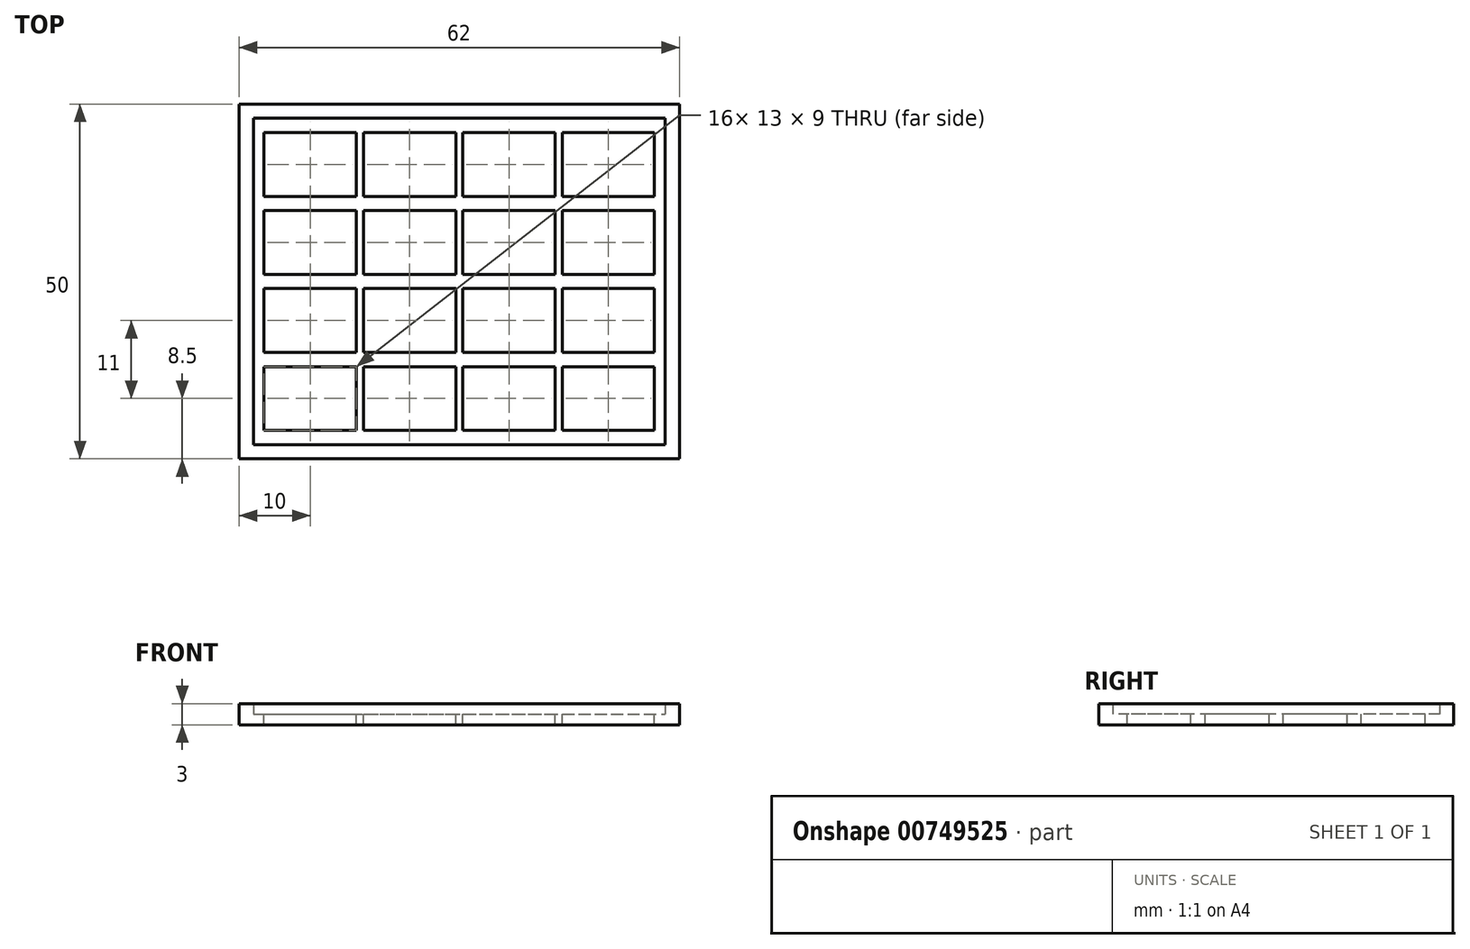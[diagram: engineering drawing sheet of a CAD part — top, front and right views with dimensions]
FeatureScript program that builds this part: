
annotation { "Feature Type Name" : "Feature", "Feature Type Description" : "" }
export const myFeature = defineFeature(function(context is Context, id is Id, definition is map)
    precondition{}
    {
        {
            var Q0;
            Q0=qCreatedBy(makeId("Top.planeOp"),FACE);
            var sketch = newSketch(context, id + "F0", { "sketchPlane" : qUnion([Q0])});
            skLineSegment(sketch, "E0.bottom", {"start": v(-29, 23) * mm, "end": v(29, 23) * mm});
            skLineSegment(sketch, "E0.top", {"start": v(-29, -23) * mm, "end": v(29, -23) * mm});
            skLineSegment(sketch, "E0.left", {"start": v(-29, 23) * mm, "end": v(-29, -23) * mm});
            skLineSegment(sketch, "E0.right", {"start": v(29, 23) * mm, "end": v(29, -23) * mm});
            skLineSegment(sketch, "E1.bottom", {"start": v(-31, 25) * mm, "end": v(31, 25) * mm});
            skLineSegment(sketch, "E1.top", {"start": v(-31, -25) * mm, "end": v(31, -25) * mm});
            skLineSegment(sketch, "E1.left", {"start": v(-31, 25) * mm, "end": v(-31, -25) * mm});
            skLineSegment(sketch, "E1.right", {"start": v(31, 25) * mm, "end": v(31, -25) * mm});
            skSolve(sketch);
        }
        {
            var Q0;
            Q0=makeQuery(id+"F0.imprint","IMPRINT",FACE,{"disambiguationData":[TD([[makeQuery(id+"F0.imprint","IMPRINT",EDGE,{"derivedFrom":sQuery(id+"F0.wireOp",EDGE,"E0.bottom")}),-1.0]])]});
            extrude(context, id + "F1", {"entities" : qUnion([Q0]), "depth" : 1.5 * mm, "offsetDistance" : 25 * mm});
        }
        {
            var Q0;
            Q0=makeQuery(id+"F1.opExtrude","CAP_FACE",FACE,{"disambiguationData":[OSD([sQuery(id+"F0.wireOp",EDGE,"E0.bottom"),sQuery(id+"F0.wireOp",EDGE,"E0.top"),sQuery(id+"F0.wireOp",EDGE,"E0.left"),sQuery(id+"F0.wireOp",EDGE,"E0.right")])],"isStart":false});
            var sketch = newSketch(context, id + "F2", { "sketchPlane" : qUnion([Q0])});
            skPoint(sketch, "E2.middle", {"position": v(0, 0) * mm});
            skLineSegment(sketch, "E3.bottom", {"start": v(-15.5, 13) * mm, "end": v(-26.5, 13) * mm});
            skLineSegment(sketch, "E3.top", {"start": v(-15.5, 20) * mm, "end": v(-26.5, 20) * mm});
            skLineSegment(sketch, "E3.left", {"start": v(-15.5, 13) * mm, "end": v(-15.5, 20) * mm});
            skLineSegment(sketch, "E3.right", {"start": v(-26.5, 13) * mm, "end": v(-26.5, 20) * mm});
            skPoint(sketch, "E3.middle", {"position": v(-21, 16.5) * mm});
            skLineSegment(sketch, "E4.1.0.0", {"start": v(-12.5, 13) * mm, "end": v(-12.5, 20) * mm});
            skLineSegment(sketch, "E4.1.0.1", {"start": v(-1.5, 13) * mm, "end": v(-1.5, 20) * mm});
            skLineSegment(sketch, "E4.1.0.2", {"start": v(-1.5, 20) * mm, "end": v(-12.5, 20) * mm});
            skPoint(sketch, "E4.1.0.3", {"position": v(-7, 16.5) * mm});
            skLineSegment(sketch, "E4.1.0.4", {"start": v(-1.5, 13) * mm, "end": v(-12.5, 13) * mm});
            skLineSegment(sketch, "E4.2.0.0", {"start": v(1.5, 13) * mm, "end": v(1.5, 20) * mm});
            skLineSegment(sketch, "E4.2.0.1", {"start": v(12.5, 13) * mm, "end": v(12.5, 20) * mm});
            skLineSegment(sketch, "E4.2.0.2", {"start": v(12.5, 20) * mm, "end": v(1.5, 20) * mm});
            skPoint(sketch, "E4.2.0.3", {"position": v(7, 16.5) * mm});
            skLineSegment(sketch, "E4.2.0.4", {"start": v(12.5, 13) * mm, "end": v(1.5, 13) * mm});
            skLineSegment(sketch, "E4.3.0.0", {"start": v(15.5, 13) * mm, "end": v(15.5, 20) * mm});
            skLineSegment(sketch, "E4.3.0.1", {"start": v(26.5, 13) * mm, "end": v(26.5, 20) * mm});
            skLineSegment(sketch, "E4.3.0.2", {"start": v(26.5, 20) * mm, "end": v(15.5, 20) * mm});
            skPoint(sketch, "E4.3.0.3", {"position": v(21, 16.5) * mm});
            skLineSegment(sketch, "E4.3.0.4", {"start": v(26.5, 13) * mm, "end": v(15.5, 13) * mm});
            skLineSegment(sketch, "E4.direction1", {"start": v(-26.5, 13) * mm, "end": v(-12.5, 13) * mm, "construction": true});
            skLineSegment(sketch, "E5.1.0.0", {"start": v(15.58, 2) * mm, "end": v(15.58, 9) * mm});
            skLineSegment(sketch, "E5.1.0.1", {"start": v(26.58, 9) * mm, "end": v(15.58, 9) * mm});
            skLineSegment(sketch, "E5.1.0.2", {"start": v(-26.42, 2) * mm, "end": v(-12.42, 2) * mm, "construction": true});
            skPoint(sketch, "E5.1.0.3", {"position": v(-20.92, 5.5) * mm});
            skLineSegment(sketch, "E5.1.0.4", {"start": v(1.58, 2) * mm, "end": v(1.58, 9) * mm});
            skLineSegment(sketch, "E5.1.0.5", {"start": v(-1.42, 2) * mm, "end": v(-12.42, 2) * mm});
            skLineSegment(sketch, "E5.1.0.6", {"start": v(-1.42, 9) * mm, "end": v(-12.42, 9) * mm});
            skLineSegment(sketch, "E5.1.0.7", {"start": v(-1.42, 2) * mm, "end": v(-1.42, 9) * mm});
            skLineSegment(sketch, "E5.1.0.8", {"start": v(-12.42, 2) * mm, "end": v(-12.42, 9) * mm});
            skLineSegment(sketch, "E5.1.0.9", {"start": v(-26.42, 2) * mm, "end": v(-26.42, 9) * mm});
            skLineSegment(sketch, "E5.1.0.10", {"start": v(-15.42, 2) * mm, "end": v(-15.42, 9) * mm});
            skLineSegment(sketch, "E5.1.0.11", {"start": v(-15.42, 9) * mm, "end": v(-26.42, 9) * mm});
            skPoint(sketch, "E5.1.0.12", {"position": v(7.08, 5.5) * mm});
            skLineSegment(sketch, "E5.1.0.13", {"start": v(12.58, 2) * mm, "end": v(1.58, 2) * mm});
            skLineSegment(sketch, "E5.1.0.14", {"start": v(12.58, 9) * mm, "end": v(1.58, 9) * mm});
            skLineSegment(sketch, "E5.1.0.15", {"start": v(12.58, 2) * mm, "end": v(12.58, 9) * mm});
            skLineSegment(sketch, "E5.1.0.16", {"start": v(26.58, 2) * mm, "end": v(26.58, 9) * mm});
            skLineSegment(sketch, "E5.1.0.17", {"start": v(26.58, 2) * mm, "end": v(15.58, 2) * mm});
            skPoint(sketch, "E5.1.0.18", {"position": v(-6.92, 5.5) * mm});
            skPoint(sketch, "E5.1.0.19", {"position": v(21.08, 5.5) * mm});
            skLineSegment(sketch, "E5.1.0.20", {"start": v(-15.42, 2) * mm, "end": v(-26.42, 2) * mm});
            skLineSegment(sketch, "E5.2.0.0", {"start": v(15.65, -9) * mm, "end": v(15.65, -2) * mm});
            skLineSegment(sketch, "E5.2.0.1", {"start": v(26.65, -2) * mm, "end": v(15.65, -2) * mm});
            skLineSegment(sketch, "E5.2.0.2", {"start": v(-26.35, -9) * mm, "end": v(-12.35, -9) * mm, "construction": true});
            skPoint(sketch, "E5.2.0.3", {"position": v(-20.85, -5.5) * mm});
            skLineSegment(sketch, "E5.2.0.4", {"start": v(1.65, -9) * mm, "end": v(1.65, -2) * mm});
            skLineSegment(sketch, "E5.2.0.5", {"start": v(-1.35, -9) * mm, "end": v(-12.35, -9) * mm});
            skLineSegment(sketch, "E5.2.0.6", {"start": v(-1.35, -2) * mm, "end": v(-12.35, -2) * mm});
            skLineSegment(sketch, "E5.2.0.7", {"start": v(-1.35, -9) * mm, "end": v(-1.35, -2) * mm});
            skLineSegment(sketch, "E5.2.0.8", {"start": v(-12.35, -9) * mm, "end": v(-12.35, -2) * mm});
            skLineSegment(sketch, "E5.2.0.9", {"start": v(-26.35, -9) * mm, "end": v(-26.35, -2) * mm});
            skLineSegment(sketch, "E5.2.0.10", {"start": v(-15.35, -9) * mm, "end": v(-15.35, -2) * mm});
            skLineSegment(sketch, "E5.2.0.11", {"start": v(-15.35, -2) * mm, "end": v(-26.35, -2) * mm});
            skPoint(sketch, "E5.2.0.12", {"position": v(7.15, -5.5) * mm});
            skLineSegment(sketch, "E5.2.0.13", {"start": v(12.65, -9) * mm, "end": v(1.65, -9) * mm});
            skLineSegment(sketch, "E5.2.0.14", {"start": v(12.65, -2) * mm, "end": v(1.65, -2) * mm});
            skLineSegment(sketch, "E5.2.0.15", {"start": v(12.65, -9) * mm, "end": v(12.65, -2) * mm});
            skLineSegment(sketch, "E5.2.0.16", {"start": v(26.65, -9) * mm, "end": v(26.65, -2) * mm});
            skLineSegment(sketch, "E5.2.0.17", {"start": v(26.65, -9) * mm, "end": v(15.65, -9) * mm});
            skPoint(sketch, "E5.2.0.18", {"position": v(-6.85, -5.5) * mm});
            skPoint(sketch, "E5.2.0.19", {"position": v(21.15, -5.5) * mm});
            skLineSegment(sketch, "E5.2.0.20", {"start": v(-15.35, -9) * mm, "end": v(-26.35, -9) * mm});
            skLineSegment(sketch, "E5.3.0.0", {"start": v(15.73, -20) * mm, "end": v(15.73, -13) * mm});
            skLineSegment(sketch, "E5.3.0.1", {"start": v(26.73, -13) * mm, "end": v(15.73, -13) * mm});
            skLineSegment(sketch, "E5.3.0.2", {"start": v(-26.27, -20) * mm, "end": v(-12.27, -20) * mm, "construction": true});
            skPoint(sketch, "E5.3.0.3", {"position": v(-20.77, -16.5) * mm});
            skLineSegment(sketch, "E5.3.0.4", {"start": v(1.73, -20) * mm, "end": v(1.73, -13) * mm});
            skLineSegment(sketch, "E5.3.0.5", {"start": v(-1.27, -20) * mm, "end": v(-12.27, -20) * mm});
            skLineSegment(sketch, "E5.3.0.6", {"start": v(-1.27, -13) * mm, "end": v(-12.27, -13) * mm});
            skLineSegment(sketch, "E5.3.0.7", {"start": v(-1.27, -20) * mm, "end": v(-1.27, -13) * mm});
            skLineSegment(sketch, "E5.3.0.8", {"start": v(-12.27, -20) * mm, "end": v(-12.27, -13) * mm});
            skLineSegment(sketch, "E5.3.0.9", {"start": v(-26.27, -20) * mm, "end": v(-26.27, -13) * mm});
            skLineSegment(sketch, "E5.3.0.10", {"start": v(-15.27, -20) * mm, "end": v(-15.27, -13) * mm});
            skLineSegment(sketch, "E5.3.0.11", {"start": v(-15.27, -13) * mm, "end": v(-26.27, -13) * mm});
            skPoint(sketch, "E5.3.0.12", {"position": v(7.23, -16.5) * mm});
            skLineSegment(sketch, "E5.3.0.13", {"start": v(12.73, -20) * mm, "end": v(1.73, -20) * mm});
            skLineSegment(sketch, "E5.3.0.14", {"start": v(12.73, -13) * mm, "end": v(1.73, -13) * mm});
            skLineSegment(sketch, "E5.3.0.15", {"start": v(12.73, -20) * mm, "end": v(12.73, -13) * mm});
            skLineSegment(sketch, "E5.3.0.16", {"start": v(26.73, -20) * mm, "end": v(26.73, -13) * mm});
            skLineSegment(sketch, "E5.3.0.17", {"start": v(26.73, -20) * mm, "end": v(15.73, -20) * mm});
            skPoint(sketch, "E5.3.0.18", {"position": v(-6.77, -16.5) * mm});
            skPoint(sketch, "E5.3.0.19", {"position": v(21.23, -16.5) * mm});
            skLineSegment(sketch, "E5.3.0.20", {"start": v(-15.27, -20) * mm, "end": v(-26.27, -20) * mm});
            skLineSegment(sketch, "E5.direction1", {"start": v(-26.5, 13) * mm, "end": v(-26.42, 2) * mm, "construction": true});
            skSolve(sketch);
        }
        {
            var Q0;
            Q0=makeQuery(id+"F2.imprint","IMPRINT",FACE,{"disambiguationData":[TD([[makeQuery(id+"F2.imprint","IMPRINT",EDGE,{"derivedFrom":sQuery(id+"F2.wireOp",EDGE,"E3.bottom")}),-1.0]])]});
            var Q1;
            Q1=makeQuery(id+"F2.imprint","IMPRINT",FACE,{"disambiguationData":[TD([[makeQuery(id+"F2.imprint","IMPRINT",EDGE,{"derivedFrom":sQuery(id+"F2.wireOp",EDGE,"E4.1.0.0")}),-1.0]])]});
            var Q2;
            Q2=makeQuery(id+"F2.imprint","IMPRINT",FACE,{"disambiguationData":[TD([[makeQuery(id+"F2.imprint","IMPRINT",EDGE,{"derivedFrom":sQuery(id+"F2.wireOp",EDGE,"E4.2.0.0")}),-1.0]])]});
            var Q3;
            Q3=makeQuery(id+"F2.imprint","IMPRINT",FACE,{"disambiguationData":[TD([[makeQuery(id+"F2.imprint","IMPRINT",EDGE,{"derivedFrom":sQuery(id+"F2.wireOp",EDGE,"E4.3.0.0")}),-1.0]])]});
            var Q4;
            Q4=makeQuery(id+"F2.imprint","IMPRINT",FACE,{"disambiguationData":[TD([[makeQuery(id+"F2.imprint","IMPRINT",EDGE,{"derivedFrom":sQuery(id+"F2.wireOp",EDGE,"E5.1.0.9")}),-1.0]])]});
            var Q5;
            Q5=makeQuery(id+"F2.imprint","IMPRINT",FACE,{"disambiguationData":[TD([[makeQuery(id+"F2.imprint","IMPRINT",EDGE,{"derivedFrom":sQuery(id+"F2.wireOp",EDGE,"E5.1.0.5")}),-1.0]])]});
            var Q6;
            Q6=makeQuery(id+"F2.imprint","IMPRINT",FACE,{"disambiguationData":[TD([[makeQuery(id+"F2.imprint","IMPRINT",EDGE,{"derivedFrom":sQuery(id+"F2.wireOp",EDGE,"E5.1.0.4")}),-1.0]])]});
            var Q7;
            Q7=makeQuery(id+"F2.imprint","IMPRINT",FACE,{"disambiguationData":[TD([[makeQuery(id+"F2.imprint","IMPRINT",EDGE,{"derivedFrom":sQuery(id+"F2.wireOp",EDGE,"E5.1.0.0")}),-1.0]])]});
            var Q8;
            Q8=makeQuery(id+"F2.imprint","IMPRINT",FACE,{"disambiguationData":[TD([[makeQuery(id+"F2.imprint","IMPRINT",EDGE,{"derivedFrom":sQuery(id+"F2.wireOp",EDGE,"E5.2.0.9")}),-1.0]])]});
            var Q9;
            Q9=makeQuery(id+"F2.imprint","IMPRINT",FACE,{"disambiguationData":[TD([[makeQuery(id+"F2.imprint","IMPRINT",EDGE,{"derivedFrom":sQuery(id+"F2.wireOp",EDGE,"E5.2.0.5")}),-1.0]])]});
            var Q10;
            Q10=makeQuery(id+"F2.imprint","IMPRINT",FACE,{"disambiguationData":[TD([[makeQuery(id+"F2.imprint","IMPRINT",EDGE,{"derivedFrom":sQuery(id+"F2.wireOp",EDGE,"E5.2.0.4")}),-1.0]])]});
            var Q11;
            Q11=makeQuery(id+"F2.imprint","IMPRINT",FACE,{"disambiguationData":[TD([[makeQuery(id+"F2.imprint","IMPRINT",EDGE,{"derivedFrom":sQuery(id+"F2.wireOp",EDGE,"E5.2.0.0")}),-1.0]])]});
            var Q12;
            Q12=makeQuery(id+"F2.imprint","IMPRINT",FACE,{"disambiguationData":[TD([[makeQuery(id+"F2.imprint","IMPRINT",EDGE,{"derivedFrom":sQuery(id+"F2.wireOp",EDGE,"E5.3.0.9")}),-1.0]])]});
            var Q13;
            Q13=makeQuery(id+"F2.imprint","IMPRINT",FACE,{"disambiguationData":[TD([[makeQuery(id+"F2.imprint","IMPRINT",EDGE,{"derivedFrom":sQuery(id+"F2.wireOp",EDGE,"E5.3.0.5")}),-1.0]])]});
            var Q14;
            Q14=makeQuery(id+"F2.imprint","IMPRINT",FACE,{"disambiguationData":[TD([[makeQuery(id+"F2.imprint","IMPRINT",EDGE,{"derivedFrom":sQuery(id+"F2.wireOp",EDGE,"E5.3.0.4")}),-1.0]])]});
            var Q15;
            Q15=makeQuery(id+"F2.imprint","IMPRINT",FACE,{"disambiguationData":[TD([[makeQuery(id+"F2.imprint","IMPRINT",EDGE,{"derivedFrom":sQuery(id+"F2.wireOp",EDGE,"E5.3.0.0")}),-1.0]])]});
            extrude(context, id + "F3", {"entities" : qUnion([Q0, Q1, Q2, Q3, Q4, Q5, Q6, Q7, Q8, Q9, Q10, Q11, Q12, Q13, Q14, Q15]), "operationType" : NewBodyOperationType.REMOVE, "endBound" : BoundingType.THROUGH_ALL, "oppositeDirection" : true, "depth" : 4 * mm, "offsetDistance" : 25 * mm});
        }
        {
            var Q0;
            Q0=makeQuery(id+"F1.opExtrude","CAP_FACE",FACE,{"disambiguationData":[OSD([sQuery(id+"F0.wireOp",EDGE,"E0.bottom"),sQuery(id+"F0.wireOp",EDGE,"E0.top"),sQuery(id+"F0.wireOp",EDGE,"E0.left"),sQuery(id+"F0.wireOp",EDGE,"E0.right")])],"isStart":false});
            var sketch = newSketch(context, id + "F4", { "sketchPlane" : qUnion([Q0])});
            skLineSegment(sketch, "E6.bottom", {"start": v(-27.5, 21) * mm, "end": v(-14.5, 21) * mm});
            skLineSegment(sketch, "E6.top", {"start": v(-27.5, 12) * mm, "end": v(-14.5, 12) * mm});
            skLineSegment(sketch, "E6.left", {"start": v(-27.5, 21) * mm, "end": v(-27.5, 12) * mm});
            skLineSegment(sketch, "E6.right", {"start": v(-14.5, 21) * mm, "end": v(-14.5, 12) * mm});
            skLineSegment(sketch, "E7.1.0.0", {"start": v(-13.5, 12) * mm, "end": v(-0.5, 12) * mm});
            skLineSegment(sketch, "E7.1.0.1", {"start": v(-13.5, 21) * mm, "end": v(-0.5, 21) * mm});
            skLineSegment(sketch, "E7.1.0.2", {"start": v(-13.5, 21) * mm, "end": v(-13.5, 12) * mm});
            skLineSegment(sketch, "E7.1.0.3", {"start": v(-0.5, 21) * mm, "end": v(-0.5, 12) * mm});
            skLineSegment(sketch, "E7.2.0.0", {"start": v(0.5, 12) * mm, "end": v(13.5, 12) * mm});
            skLineSegment(sketch, "E7.2.0.1", {"start": v(0.5, 21) * mm, "end": v(13.5, 21) * mm});
            skLineSegment(sketch, "E7.2.0.2", {"start": v(0.5, 21) * mm, "end": v(0.5, 12) * mm});
            skLineSegment(sketch, "E7.2.0.3", {"start": v(13.5, 21) * mm, "end": v(13.5, 12) * mm});
            skLineSegment(sketch, "E7.3.0.0", {"start": v(14.5, 12) * mm, "end": v(27.5, 12) * mm});
            skLineSegment(sketch, "E7.3.0.1", {"start": v(14.5, 21) * mm, "end": v(27.5, 21) * mm});
            skLineSegment(sketch, "E7.3.0.2", {"start": v(14.5, 21) * mm, "end": v(14.5, 12) * mm});
            skLineSegment(sketch, "E7.3.0.3", {"start": v(27.5, 21) * mm, "end": v(27.5, 12) * mm});
            skLineSegment(sketch, "E7.direction1", {"start": v(-27.5, 12) * mm, "end": v(-13.5, 12) * mm, "construction": true});
            skLineSegment(sketch, "E8.1.0.0", {"start": v(14.5, 1) * mm, "end": v(27.5, 1) * mm});
            skLineSegment(sketch, "E8.1.0.1", {"start": v(13.5, 10) * mm, "end": v(13.5, 1) * mm});
            skLineSegment(sketch, "E8.1.0.2", {"start": v(0.5, 10) * mm, "end": v(0.5, 1) * mm});
            skLineSegment(sketch, "E8.1.0.3", {"start": v(0.5, 10) * mm, "end": v(13.5, 10) * mm});
            skLineSegment(sketch, "E8.1.0.4", {"start": v(0.5, 1) * mm, "end": v(13.5, 1) * mm});
            skLineSegment(sketch, "E8.1.0.5", {"start": v(-0.5, 10) * mm, "end": v(-0.5, 1) * mm});
            skLineSegment(sketch, "E8.1.0.6", {"start": v(-13.5, 10) * mm, "end": v(-13.5, 1) * mm});
            skLineSegment(sketch, "E8.1.0.7", {"start": v(-13.5, 10) * mm, "end": v(-0.5, 10) * mm});
            skLineSegment(sketch, "E8.1.0.8", {"start": v(-14.5, 10) * mm, "end": v(-14.5, 1) * mm});
            skLineSegment(sketch, "E8.1.0.9", {"start": v(-27.5, 10) * mm, "end": v(-27.5, 1) * mm});
            skLineSegment(sketch, "E8.1.0.10", {"start": v(-27.5, 10) * mm, "end": v(-14.5, 10) * mm});
            skLineSegment(sketch, "E8.1.0.11", {"start": v(27.5, 10) * mm, "end": v(27.5, 1) * mm});
            skLineSegment(sketch, "E8.1.0.12", {"start": v(14.5, 10) * mm, "end": v(14.5, 1) * mm});
            skLineSegment(sketch, "E8.1.0.13", {"start": v(14.5, 10) * mm, "end": v(27.5, 10) * mm});
            skLineSegment(sketch, "E8.1.0.14", {"start": v(-27.5, 1) * mm, "end": v(-13.5, 1) * mm, "construction": true});
            skLineSegment(sketch, "E8.1.0.15", {"start": v(-27.5, 1) * mm, "end": v(-14.5, 1) * mm});
            skLineSegment(sketch, "E8.1.0.16", {"start": v(-13.5, 1) * mm, "end": v(-0.5, 1) * mm});
            skLineSegment(sketch, "E8.2.0.0", {"start": v(14.5, -10) * mm, "end": v(27.5, -10) * mm});
            skLineSegment(sketch, "E8.2.0.1", {"start": v(13.5, -1) * mm, "end": v(13.5, -10) * mm});
            skLineSegment(sketch, "E8.2.0.2", {"start": v(0.5, -1) * mm, "end": v(0.5, -10) * mm});
            skLineSegment(sketch, "E8.2.0.3", {"start": v(0.5, -1) * mm, "end": v(13.5, -1) * mm});
            skLineSegment(sketch, "E8.2.0.4", {"start": v(0.5, -10) * mm, "end": v(13.5, -10) * mm});
            skLineSegment(sketch, "E8.2.0.5", {"start": v(-0.5, -1) * mm, "end": v(-0.5, -10) * mm});
            skLineSegment(sketch, "E8.2.0.6", {"start": v(-13.5, -1) * mm, "end": v(-13.5, -10) * mm});
            skLineSegment(sketch, "E8.2.0.7", {"start": v(-13.5, -1) * mm, "end": v(-0.5, -1) * mm});
            skLineSegment(sketch, "E8.2.0.8", {"start": v(-14.5, -1) * mm, "end": v(-14.5, -10) * mm});
            skLineSegment(sketch, "E8.2.0.9", {"start": v(-27.5, -1) * mm, "end": v(-27.5, -10) * mm});
            skLineSegment(sketch, "E8.2.0.10", {"start": v(-27.5, -1) * mm, "end": v(-14.5, -1) * mm});
            skLineSegment(sketch, "E8.2.0.11", {"start": v(27.5, -1) * mm, "end": v(27.5, -10) * mm});
            skLineSegment(sketch, "E8.2.0.12", {"start": v(14.5, -1) * mm, "end": v(14.5, -10) * mm});
            skLineSegment(sketch, "E8.2.0.13", {"start": v(14.5, -1) * mm, "end": v(27.5, -1) * mm});
            skLineSegment(sketch, "E8.2.0.14", {"start": v(-27.5, -10) * mm, "end": v(-13.5, -10) * mm, "construction": true});
            skLineSegment(sketch, "E8.2.0.15", {"start": v(-27.5, -10) * mm, "end": v(-14.5, -10) * mm});
            skLineSegment(sketch, "E8.2.0.16", {"start": v(-13.5, -10) * mm, "end": v(-0.5, -10) * mm});
            skLineSegment(sketch, "E8.3.0.0", {"start": v(14.5, -21) * mm, "end": v(27.5, -21) * mm});
            skLineSegment(sketch, "E8.3.0.1", {"start": v(13.5, -12) * mm, "end": v(13.5, -21) * mm});
            skLineSegment(sketch, "E8.3.0.2", {"start": v(0.5, -12) * mm, "end": v(0.5, -21) * mm});
            skLineSegment(sketch, "E8.3.0.3", {"start": v(0.5, -12) * mm, "end": v(13.5, -12) * mm});
            skLineSegment(sketch, "E8.3.0.4", {"start": v(0.5, -21) * mm, "end": v(13.5, -21) * mm});
            skLineSegment(sketch, "E8.3.0.5", {"start": v(-0.5, -12) * mm, "end": v(-0.5, -21) * mm});
            skLineSegment(sketch, "E8.3.0.6", {"start": v(-13.5, -12) * mm, "end": v(-13.5, -21) * mm});
            skLineSegment(sketch, "E8.3.0.7", {"start": v(-13.5, -12) * mm, "end": v(-0.5, -12) * mm});
            skLineSegment(sketch, "E8.3.0.8", {"start": v(-14.5, -12) * mm, "end": v(-14.5, -21) * mm});
            skLineSegment(sketch, "E8.3.0.9", {"start": v(-27.5, -12) * mm, "end": v(-27.5, -21) * mm});
            skLineSegment(sketch, "E8.3.0.10", {"start": v(-27.5, -12) * mm, "end": v(-14.5, -12) * mm});
            skLineSegment(sketch, "E8.3.0.11", {"start": v(27.5, -12) * mm, "end": v(27.5, -21) * mm});
            skLineSegment(sketch, "E8.3.0.12", {"start": v(14.5, -12) * mm, "end": v(14.5, -21) * mm});
            skLineSegment(sketch, "E8.3.0.13", {"start": v(14.5, -12) * mm, "end": v(27.5, -12) * mm});
            skLineSegment(sketch, "E8.3.0.14", {"start": v(-27.5, -21) * mm, "end": v(-13.5, -21) * mm, "construction": true});
            skLineSegment(sketch, "E8.3.0.15", {"start": v(-27.5, -21) * mm, "end": v(-14.5, -21) * mm});
            skLineSegment(sketch, "E8.3.0.16", {"start": v(-13.5, -21) * mm, "end": v(-0.5, -21) * mm});
            skLineSegment(sketch, "E8.direction1", {"start": v(-27.5, 12) * mm, "end": v(-27.5, 1) * mm, "construction": true});
            skSolve(sketch);
        }
        {
            var Q0;
            Q0=makeQuery(id+"F4.imprint","IMPRINT",FACE,{"disambiguationData":[TD([[makeQuery(id+"F4.imprint","IMPRINT",EDGE,{"derivedFrom":sQuery(id+"F4.wireOp",EDGE,"E6.bottom")}),-1.0]])]});
            var Q1;
            Q1=makeQuery(id+"F4.imprint","IMPRINT",FACE,{"disambiguationData":[TD([[makeQuery(id+"F4.imprint","IMPRINT",EDGE,{"derivedFrom":sQuery(id+"F4.wireOp",EDGE,"E7.1.0.0")}),1.0]])]});
            var Q2;
            Q2=makeQuery(id+"F4.imprint","IMPRINT",FACE,{"disambiguationData":[TD([[makeQuery(id+"F4.imprint","IMPRINT",EDGE,{"derivedFrom":sQuery(id+"F4.wireOp",EDGE,"E7.2.0.0")}),1.0]])]});
            var Q3;
            Q3=makeQuery(id+"F4.imprint","IMPRINT",FACE,{"disambiguationData":[TD([[makeQuery(id+"F4.imprint","IMPRINT",EDGE,{"derivedFrom":sQuery(id+"F4.wireOp",EDGE,"E7.3.0.0")}),1.0]])]});
            var Q4;
            Q4=makeQuery(id+"F4.imprint","IMPRINT",FACE,{"disambiguationData":[TD([[makeQuery(id+"F4.imprint","IMPRINT",EDGE,{"derivedFrom":sQuery(id+"F4.wireOp",EDGE,"E8.1.0.8")}),-1.0]])]});
            var Q5;
            Q5=makeQuery(id+"F4.imprint","IMPRINT",FACE,{"disambiguationData":[TD([[makeQuery(id+"F4.imprint","IMPRINT",EDGE,{"derivedFrom":sQuery(id+"F4.wireOp",EDGE,"E8.1.0.1")}),-1.0]])]});
            var Q6;
            Q6=makeQuery(id+"F4.imprint","IMPRINT",FACE,{"disambiguationData":[TD([[makeQuery(id+"F4.imprint","IMPRINT",EDGE,{"derivedFrom":sQuery(id+"F4.wireOp",EDGE,"E8.1.0.5")}),-1.0]])]});
            var Q7;
            Q7=makeQuery(id+"F4.imprint","IMPRINT",FACE,{"disambiguationData":[TD([[makeQuery(id+"F4.imprint","IMPRINT",EDGE,{"derivedFrom":sQuery(id+"F4.wireOp",EDGE,"E8.1.0.0")}),1.0]])]});
            var Q8;
            Q8=makeQuery(id+"F4.imprint","IMPRINT",FACE,{"disambiguationData":[TD([[makeQuery(id+"F4.imprint","IMPRINT",EDGE,{"derivedFrom":sQuery(id+"F4.wireOp",EDGE,"E8.2.0.8")}),-1.0]])]});
            var Q9;
            Q9=makeQuery(id+"F4.imprint","IMPRINT",FACE,{"disambiguationData":[TD([[makeQuery(id+"F4.imprint","IMPRINT",EDGE,{"derivedFrom":sQuery(id+"F4.wireOp",EDGE,"E8.2.0.5")}),-1.0]])]});
            var Q10;
            Q10=makeQuery(id+"F4.imprint","IMPRINT",FACE,{"disambiguationData":[TD([[makeQuery(id+"F4.imprint","IMPRINT",EDGE,{"derivedFrom":sQuery(id+"F4.wireOp",EDGE,"E8.2.0.1")}),-1.0]])]});
            var Q11;
            Q11=makeQuery(id+"F4.imprint","IMPRINT",FACE,{"disambiguationData":[TD([[makeQuery(id+"F4.imprint","IMPRINT",EDGE,{"derivedFrom":sQuery(id+"F4.wireOp",EDGE,"E8.2.0.0")}),1.0]])]});
            var Q12;
            Q12=makeQuery(id+"F4.imprint","IMPRINT",FACE,{"disambiguationData":[TD([[makeQuery(id+"F4.imprint","IMPRINT",EDGE,{"derivedFrom":sQuery(id+"F4.wireOp",EDGE,"E8.3.0.8")}),-1.0]])]});
            var Q13;
            Q13=makeQuery(id+"F4.imprint","IMPRINT",FACE,{"disambiguationData":[TD([[makeQuery(id+"F4.imprint","IMPRINT",EDGE,{"derivedFrom":sQuery(id+"F4.wireOp",EDGE,"E8.3.0.5")}),-1.0]])]});
            var Q14;
            Q14=makeQuery(id+"F4.imprint","IMPRINT",FACE,{"disambiguationData":[TD([[makeQuery(id+"F4.imprint","IMPRINT",EDGE,{"derivedFrom":sQuery(id+"F4.wireOp",EDGE,"E8.3.0.1")}),-1.0]])]});
            var Q15;
            Q15=makeQuery(id+"F4.imprint","IMPRINT",FACE,{"disambiguationData":[TD([[makeQuery(id+"F4.imprint","IMPRINT",EDGE,{"derivedFrom":sQuery(id+"F4.wireOp",EDGE,"E8.3.0.0")}),1.0]])]});
            extrude(context, id + "F5", {"entities" : qUnion([Q0, Q1, Q2, Q3, Q4, Q5, Q6, Q7, Q8, Q9, Q10, Q11, Q12, Q13, Q14, Q15]), "operationType" : NewBodyOperationType.REMOVE, "endBound" : BoundingType.THROUGH_ALL, "oppositeDirection" : true, "depth" : 0.5 * mm, "offsetDistance" : 25 * mm});
        }
        {
            var Q0;
            Q0=makeQuery(id+"F0.imprint","IMPRINT",FACE,{"disambiguationData":[TD([[makeQuery(id+"F0.imprint","IMPRINT",EDGE,{"derivedFrom":sQuery(id+"F0.wireOp",EDGE,"E0.bottom")}),1.0]])]});
            extrude(context, id + "F6", {"entities" : qUnion([Q0]), "operationType" : NewBodyOperationType.ADD, "depth" : 3 * mm, "offsetDistance" : 25 * mm});
        }
    });
